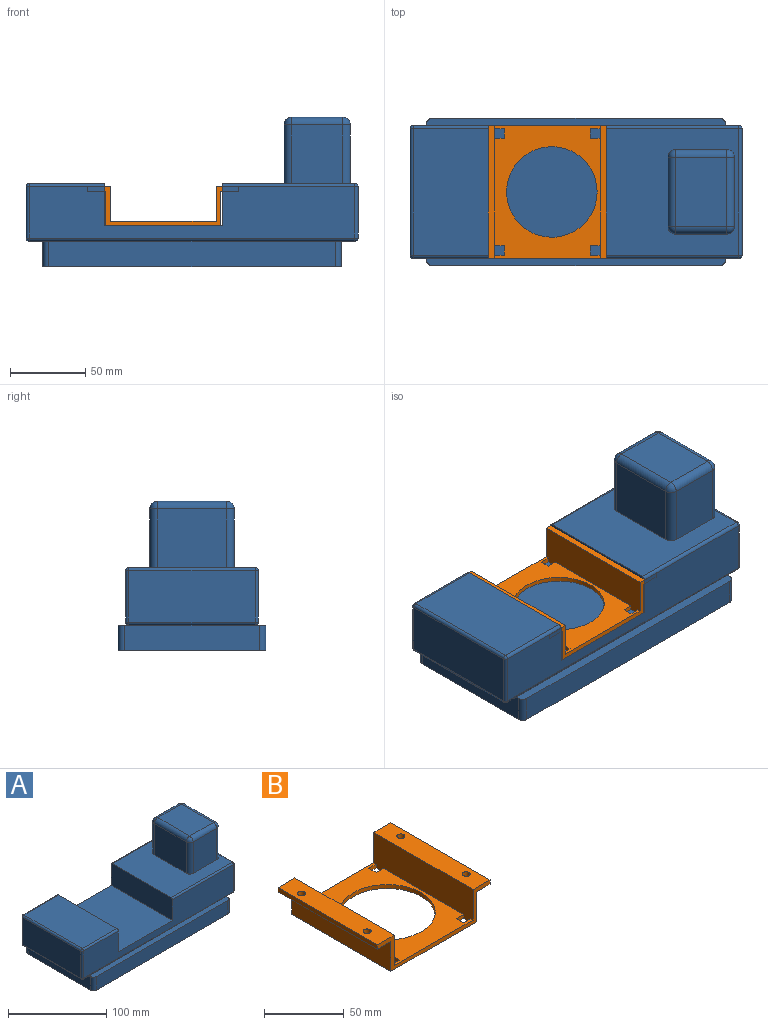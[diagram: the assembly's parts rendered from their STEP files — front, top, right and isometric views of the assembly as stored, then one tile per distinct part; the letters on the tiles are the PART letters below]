
ASSEMBLY  parts=2 mates=1
PART A: 61 faces, bbox 220x98x99 mm
  f0: plane 198x7mm, normal (0,0,1), area 1379.1mm2, adj f2,f3,f4,f7,f8,f37
  f1: plane 198x7mm, normal (0,0,1), area 1379.1mm2, adj f2,f4,f5,f9,f10,f29
  f2: plane 90x17mm, normal (-1,0,0), area 1530mm2, adj f0,f1,f6,f7,f10,f11
  f3: plane 190x17mm, normal (0,-1,0), area 3230mm2, adj f0,f6,f7,f8
  f4: plane 90x17mm, normal (1,0,0), area 1530mm2, adj f0,f1,f6,f8,f9,f18
  f5: plane 190x17mm, normal (0,1,0), area 3230mm2, adj f1,f6,f9,f10
  f6: plane 198x98mm, normal (0,0,-1), area 19390.3mm2, adj f2,f3,f4,f5,f7,f8,f9,f10
  f7: cylinder r=4mm len=17mm, axis (0,0,-1), area 106.8mm2, adj f0,f2,f3,f6
  f8: cylinder r=4mm len=17mm, axis (0,0,1), area 106.8mm2, adj f0,f3,f4,f6
  f9: cylinder r=4mm len=17mm, axis (0,0,-1), area 106.8mm2, adj f1,f4,f5,f6
  f10: cylinder r=4mm len=17mm, axis (0,0,1), area 106.8mm2, adj f1,f2,f5,f6
  f11: plane 84x9mm, normal (0,0,-1), area 756mm2, adj f2,f29,f30,f37
  f12: plane 88x84mm, normal (0,0,1), area 4949.5mm2, adj f19,f34,f40,f43,f44,f45,f46,f47
  f13: plane 216x34mm, normal (0,-1,0), area 5316mm2, adj f19,f20,f21,f26,f31,f37,f41,f43
  f14: plane 216x34mm, normal (0,1,0), area 5316mm2, adj f19,f20,f21,f22,f24,f29,f34,f35
  f15: plane 84x34mm, normal (-1,0,0), area 2856mm2, adj f24,f25,f30,f31
  f16: plane 84x34mm, normal (1,0,0), area 2856mm2, adj f35,f36,f40,f41
  f17: plane 84x50mm, normal (0,0,1), area 4200mm2, adj f20,f22,f25,f26
  f18: plane 84x9mm, normal (0,0,-1), area 756mm2, adj f4,f29,f36,f37
  f19: plane 88x28mm, normal (-1,0,0), area 2462.3mm2, adj f12,f13,f14,f21,f34,f43
  f20: plane 88x28mm, normal (1,0,0), area 2462.3mm2, adj f13,f14,f17,f21,f22,f26
  f21: plane 88x78mm, normal (0,0,1), area 6864mm2, adj f13,f14,f19,f20
  f22: cylinder r=2mm len=50mm, axis (1,0,0), area 157.1mm2, adj f14,f17,f20,f23
  f23: sphere r=2mm, area 6.3mm2, adj f22,f24,f25
  f24: cylinder r=2mm len=34mm, axis (0,0,1), area 106.8mm2, adj f14,f15,f23,f27
  f25: cylinder r=2mm len=84mm, axis (0,1,0), area 263.9mm2, adj f15,f17,f23,f28
  f26: cylinder r=2mm len=50mm, axis (-1,0,0), area 157.1mm2, adj f13,f17,f20,f28
  f27: sphere r=2mm, area 6.3mm2, adj f24,f29,f30
  f28: sphere r=2mm, area 6.3mm2, adj f25,f26,f31
  f29: cylinder r=2mm len=216mm, axis (-1,0,0), area 678.6mm2, adj f1,f11,f14,f18,f27,f32
  f30: cylinder r=2mm len=84mm, axis (0,-1,0), area 263.9mm2, adj f11,f15,f27,f33
  f31: cylinder r=2mm len=34mm, axis (0,0,-1), area 106.8mm2, adj f13,f15,f28,f33
  f32: sphere r=2mm, area 6.3mm2, adj f29,f35,f36
  f33: sphere r=2mm, area 6.3mm2, adj f30,f31,f37
  f34: cylinder r=2mm len=88mm, axis (1,0,0), area 276.5mm2, adj f12,f14,f19,f38
  f35: cylinder r=2mm len=34mm, axis (0,0,-1), area 106.8mm2, adj f14,f16,f32,f38
  f36: cylinder r=2mm len=84mm, axis (0,1,0), area 263.9mm2, adj f16,f18,f32,f39
  f37: cylinder r=2mm len=216mm, axis (1,0,0), area 678.6mm2, adj f0,f11,f13,f18,f33,f39
  f38: sphere r=2mm, area 6.3mm2, adj f34,f35,f40
  f39: sphere r=2mm, area 6.3mm2, adj f36,f37,f41
  f40: cylinder r=2mm len=84mm, axis (0,-1,0), area 263.9mm2, adj f12,f16,f38,f42
  f41: cylinder r=2mm len=34mm, axis (0,0,1), area 106.8mm2, adj f13,f16,f39,f42
  f42: sphere r=2mm, area 6.3mm2, adj f40,f41,f43
  f43: cylinder r=2mm len=88mm, axis (-1,0,0), area 276.5mm2, adj f12,f13,f19,f42
  f44: plane 39x34mm, normal (0,-1,0), area 1326mm2, adj f12,f51,f57,f60
  f45: plane 46x39mm, normal (1,0,0), area 1794mm2, adj f12,f54,f58,f60
  f46: plane 39x34mm, normal (0,1,0), area 1326mm2, adj f12,f49,f53,f54
  f47: plane 46x39mm, normal (-1,0,0), area 1794mm2, adj f12,f49,f51,f52
  f48: plane 46x34mm, normal (0,0,1), area 1564mm2, adj f52,f53,f57,f58
  f49: cylinder r=5mm len=39mm, axis (0,0,-1), area 306.3mm2, adj f12,f46,f47,f50
  f50: sphere r=5mm, area 39.3mm2, adj f49,f52,f53
  f51: cylinder r=5mm len=39mm, axis (0,0,1), area 306.3mm2, adj f12,f44,f47,f55
  f52: cylinder r=5mm len=46mm, axis (0,1,0), area 361.3mm2, adj f47,f48,f50,f55
  f53: cylinder r=5mm len=34mm, axis (1,0,0), area 267mm2, adj f46,f48,f50,f56
  f54: cylinder r=5mm len=39mm, axis (0,0,1), area 306.3mm2, adj f12,f45,f46,f56
  f55: sphere r=5mm, area 39.3mm2, adj f51,f52,f57
  f56: sphere r=5mm, area 39.3mm2, adj f53,f54,f58
  f57: cylinder r=5mm len=34mm, axis (-1,0,0), area 267mm2, adj f44,f48,f55,f59
  f58: cylinder r=5mm len=46mm, axis (0,-1,0), area 361.3mm2, adj f45,f48,f56,f59
  f59: sphere r=5mm, area 39.3mm2, adj f57,f58,f60
  f60: cylinder r=5mm len=39mm, axis (0,0,-1), area 306.3mm2, adj f12,f44,f45,f59
PART B: 31 faces, bbox 100x88x26.3 mm
  f0: plane 88x70mm, normal (0,0,1), area 3163.6mm2, adj f2,f3,f12,f13,f18,f19,f20,f21
  f1: plane 88x76mm, normal (0,0,-1), area 3691.6mm2, adj f2,f3,f7,f8,f12,f13,f18,f19
  f2: plane 88x26.33mm, normal (-1,0,0), area 2092.1mm2, adj f0,f1,f11,f12,f13,f22,f24,f25
  f3: plane 88x26.33mm, normal (1,0,0), area 2092.1mm2, adj f0,f1,f4,f12,f13,f19,f21,f28
  f4: plane 88x15mm, normal (0,0,1), area 1280.7mm2, adj f3,f5,f12,f13,f16,f17
  f5: plane 88x3.33mm, normal (-1,0,0), area 293.1mm2, adj f4,f6,f12,f13
  f6: plane 88x12mm, normal (0,0,-1), area 1016.7mm2, adj f5,f7,f12,f13,f16,f17
  f7: plane 88x23mm, normal (-1,0,0), area 2024mm2, adj f1,f6,f12,f13
  f8: plane 88x23mm, normal (1,0,0), area 2024mm2, adj f1,f9,f12,f13
  f9: plane 88x12mm, normal (0,0,-1), area 1016.7mm2, adj f8,f10,f12,f13,f14,f15
  f10: plane 88x3.33mm, normal (1,0,0), area 293.1mm2, adj f9,f11,f12,f13
  f11: plane 88x15mm, normal (0,0,1), area 1280.7mm2, adj f2,f10,f12,f13,f14,f15
  f12: plane 100x26.33mm, normal (0,-1,0), area 447.9mm2, adj f0,f1,f2,f3,f4,f5,f6,f7
  f13: plane 100x26.33mm, normal (0,1,0), area 447.9mm2, adj f0,f1,f2,f3,f4,f5,f6,f7
  f14: cylinder r=2.5mm len=5mm, axis (0,0,1), area 52.3mm2, adj f9,f11
  f15: cylinder r=2.5mm len=5mm, axis (0,0,1), area 52.3mm2, adj f9,f11
  f16: cylinder r=2.5mm len=5mm, axis (0,0,1), area 52.3mm2, adj f4,f6
  f17: cylinder r=2.5mm len=5mm, axis (0,0,1), area 52.3mm2, adj f4,f6
  f18: cylinder r=30mm len=60mm, axis (0,0,1), area 565.5mm2, adj f0,f1
  f19: plane 6.5x3mm, normal (0,1,0), area 19.5mm2, adj f0,f1,f3,f20
  f20: plane 6.5x3mm, normal (-1,0,0), area 19.5mm2, adj f0,f1,f19,f21
  f21: plane 6.5x3mm, normal (0,-1,0), area 19.5mm2, adj f0,f1,f3,f20
  f22: plane 6.5x3mm, normal (0,1,0), area 19.5mm2, adj f0,f1,f2,f23
  f23: plane 6.5x3mm, normal (1,0,0), area 19.5mm2, adj f0,f1,f22,f24
  f24: plane 6.5x3mm, normal (0,-1,0), area 19.5mm2, adj f0,f1,f2,f23
  f25: plane 6.5x3mm, normal (0,1,0), area 19.5mm2, adj f0,f1,f2,f27
  f26: plane 6.5x3mm, normal (0,-1,0), area 19.5mm2, adj f0,f1,f2,f27
  f27: plane 6.5x3mm, normal (1,0,0), area 19.5mm2, adj f0,f1,f25,f26
  f28: plane 6.5x3mm, normal (0,1,0), area 19.5mm2, adj f0,f1,f3,f29
  f29: plane 6.5x3mm, normal (-1,0,0), area 19.5mm2, adj f0,f1,f28,f30
  f30: plane 6.5x3mm, normal (0,-1,0), area 19.5mm2, adj f0,f1,f3,f29
PLACE A t=(-7,0,5.25)mm
PLACE B t=(-14.02,-4.81,37.46)mm
MATE fastened B.f1 <-> A.f21  axis (0,0,1) through (-15.99,-4.81,32.25)mm
